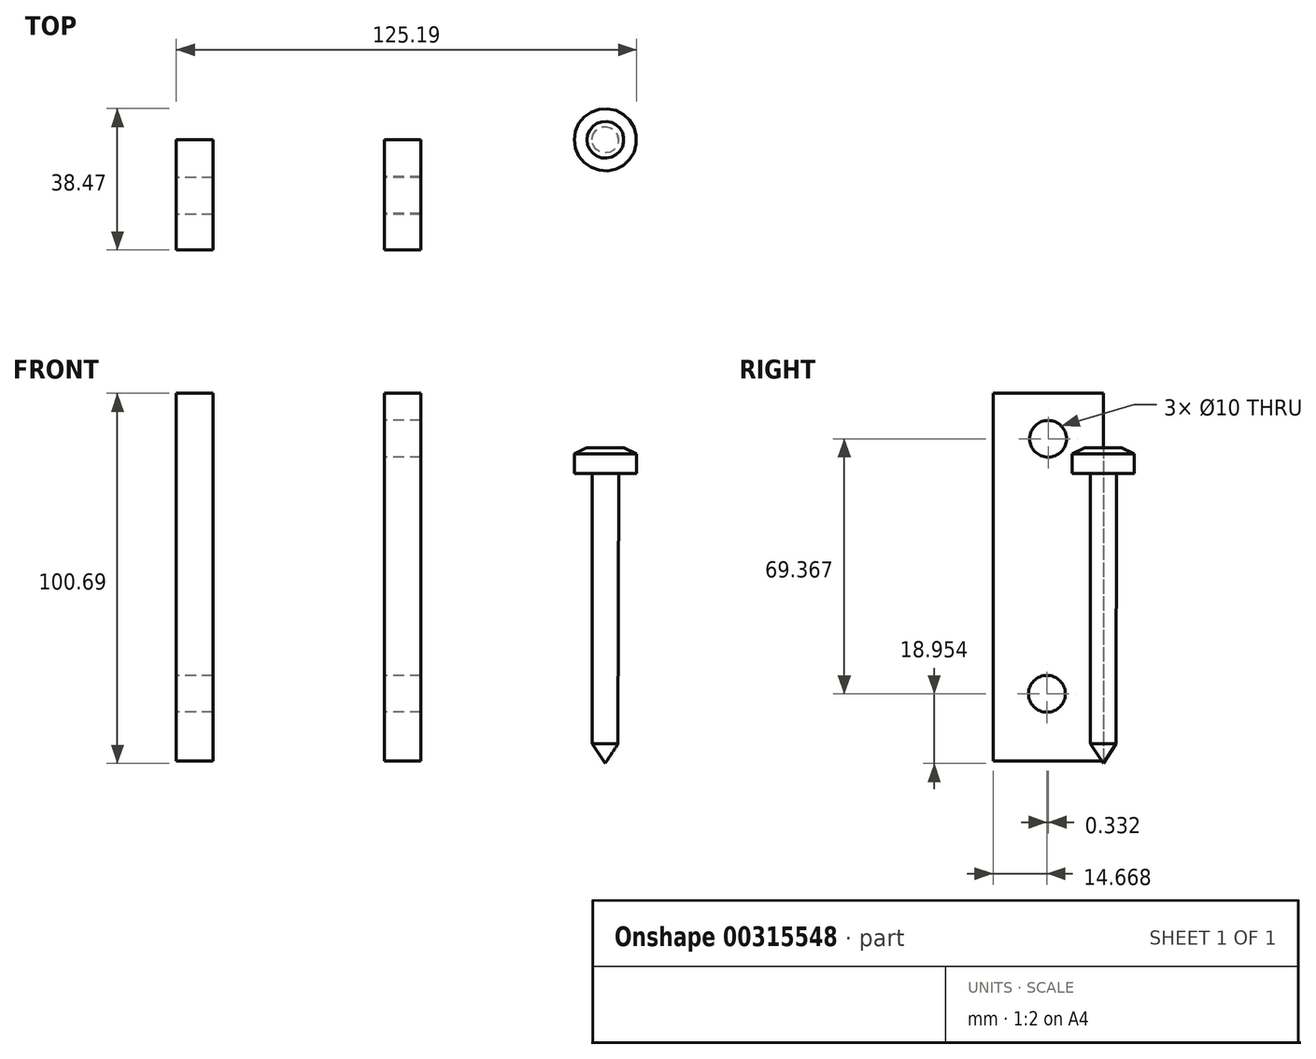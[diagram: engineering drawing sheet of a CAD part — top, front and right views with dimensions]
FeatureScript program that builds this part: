
annotation { "Feature Type Name" : "Feature", "Feature Type Description" : "" }
export const myFeature = defineFeature(function(context is Context, id is Id, definition is map)
    precondition{}
    {
        {
            var Q0;
            Q0=qCreatedBy(makeId("Front.planeOp"),FACE);
            var sketch = newSketch(context, id + "F0", { "sketchPlane" : qUnion([Q0])});
            skLineSegment(sketch, "E0.bottom", {"start": v(-41.92, 62.15) * mm, "end": v(-51.92, 62.15) * mm});
            skLineSegment(sketch, "E0.top", {"start": v(-41.92, -37.85) * mm, "end": v(-51.92, -37.85) * mm});
            skLineSegment(sketch, "E0.left", {"start": v(-41.92, 62.15) * mm, "end": v(-41.92, -37.85) * mm});
            skLineSegment(sketch, "E0.right", {"start": v(-51.92, 62.15) * mm, "end": v(-51.92, -37.85) * mm});
            skLineSegment(sketch, "E1.bottom", {"start": v(14.65, 62.15) * mm, "end": v(4.65, 62.15) * mm});
            skLineSegment(sketch, "E1.top", {"start": v(14.65, -37.85) * mm, "end": v(4.65, -37.85) * mm});
            skLineSegment(sketch, "E1.left", {"start": v(14.65, 62.15) * mm, "end": v(14.65, -37.85) * mm});
            skLineSegment(sketch, "E1.right", {"start": v(4.65, 62.15) * mm, "end": v(4.65, -37.85) * mm});
            skSolve(sketch);
        }
        {
            var Q0;
            Q0=makeQuery(id+"F0.imprint","IMPRINT",FACE,{"disambiguationData":[TD([[makeQuery(id+"F0.imprint","IMPRINT",EDGE,{"derivedFrom":sQuery(id+"F0.wireOp",EDGE,"E1.bottom")}),1.0]])]});
            var Q1;
            Q1=makeQuery(id+"F0.imprint","IMPRINT",FACE,{"disambiguationData":[TD([[makeQuery(id+"F0.imprint","IMPRINT",EDGE,{"derivedFrom":sQuery(id+"F0.wireOp",EDGE,"E0.bottom")}),1.0]])]});
            extrude(context, id + "F1", {"entities" : qUnion([Q0, Q1]), "depth" : 30 * mm});
        }
        {
            var Q0;
            Q0=makeQuery(id+"F1.opExtrude","SWEPT_FACE",FACE,{"disambiguationData":[OSD([sQuery(id+"F0.wireOp",EDGE,"E0.right")])]});
            var sketch = newSketch(context, id + "F2", { "sketchPlane" : qUnion([Q0])});
            skCircle(sketch, "E2", {"center": v(15.33, -19.59) * mm, "radius": 5 * mm});
            skSolve(sketch);
        }
        {
            var Q0;
            Q0=makeQuery(id+"F2.imprint","IMPRINT",FACE,{"disambiguationData":[TD([[makeQuery(id+"F2.imprint","IMPRINT",EDGE,{"derivedFrom":sQuery(id+"F2.wireOp",EDGE,"E2")}),1.0]])]});
            var Q1;
            Q1=sQuery(id+"F2.wireOp",EDGE,"E2");
            extrude(context, id + "F3", {"entities" : qUnion([Q0]), "operationType" : NewBodyOperationType.REMOVE, "surfaceEntities" : qUnion([Q1]), "endBound" : BoundingType.THROUGH_ALL, "oppositeDirection" : true, "depth" : 30 * mm});
        }
        {
            var Q0;
            Q0=qCreatedBy(makeId("Front.planeOp"),FACE);
            var sketch = newSketch(context, id + "F4", { "sketchPlane" : qUnion([Q0])});
            skFitSpline(sketch, "E3", {"points": [v(64.8, 47.4) * mm, v(59.8, 47.4) * mm], "startDerivative": vector(-5, 0) * mm, "endDerivative": vector(-5, 0) * mm});
            skLineSegment(sketch, "E4", {"start": v(59.8, 47.4) * mm, "end": v(56.33, 45.72) * mm});
            skLineSegment(sketch, "E5", {"start": v(56.33, 45.72) * mm, "end": v(56.33, 42.56) * mm});
            skLineSegment(sketch, "E6", {"start": v(56.33, 42.56) * mm, "end": v(56.33, 40.35) * mm});
            skLineSegment(sketch, "E7", {"start": v(56.33, 40.35) * mm, "end": v(61.22, 40.35) * mm});
            skLineSegment(sketch, "E8", {"start": v(61.22, 40.35) * mm, "end": v(61.22, -6.23) * mm});
            skLineSegment(sketch, "E9", {"start": v(64.72, -38.54) * mm, "end": v(64.8, 47.4) * mm});
            skLineSegment(sketch, "E10", {"start": v(61.22, -6.23) * mm, "end": v(61.22, -33.2) * mm});
            skLineSegment(sketch, "E11", {"start": v(61.22, -33.2) * mm, "end": v(64.72, -38.54) * mm});
            skSolve(sketch);
        }
        {
            var Q0;
            Q0=makeQuery(id+"F4.imprint","IMPRINT",FACE,{"disambiguationData":[TD([[makeQuery(id+"F4.imprint","IMPRINT",EDGE,{"derivedFrom":sQuery(id+"F4.wireOp",EDGE,"E3")}),1.0]])]});
            var Q1;
            Q1=sQuery(id+"F4.wireOp",EDGE,"E9");
            revolve(context, id + "F5", {"entities" : qUnion([Q0]), "axis" : qUnion([Q1]), "revolveType" : RevolveType.FULL});
        }
        {
            var Q0;
            Q0=makeQuery(id+"F1.opExtrude","SWEPT_FACE",FACE,{"disambiguationData":[OSD([sQuery(id+"F0.wireOp",EDGE,"E1.right")])]});
            var sketch = newSketch(context, id + "F6", { "sketchPlane" : qUnion([Q0])});
            skCircle(sketch, "E12", {"center": v(15, 49.78) * mm, "radius": 5 * mm});
            skPoint(sketch, "E12.centerSnap0", {"position": v(15, 62.15) * mm});
            skSolve(sketch);
        }
        {
            var Q0;
            Q0=makeQuery(id+"F6.imprint","IMPRINT",FACE,{"disambiguationData":[TD([[makeQuery(id+"F6.imprint","IMPRINT",EDGE,{"derivedFrom":sQuery(id+"F6.wireOp",EDGE,"E12")}),1.0]])]});
            extrude(context, id + "F7", {"entities" : qUnion([Q0]), "operationType" : NewBodyOperationType.REMOVE, "endBound" : BoundingType.THROUGH_ALL, "oppositeDirection" : true, "depth" : 25 * mm});
        }
    });
